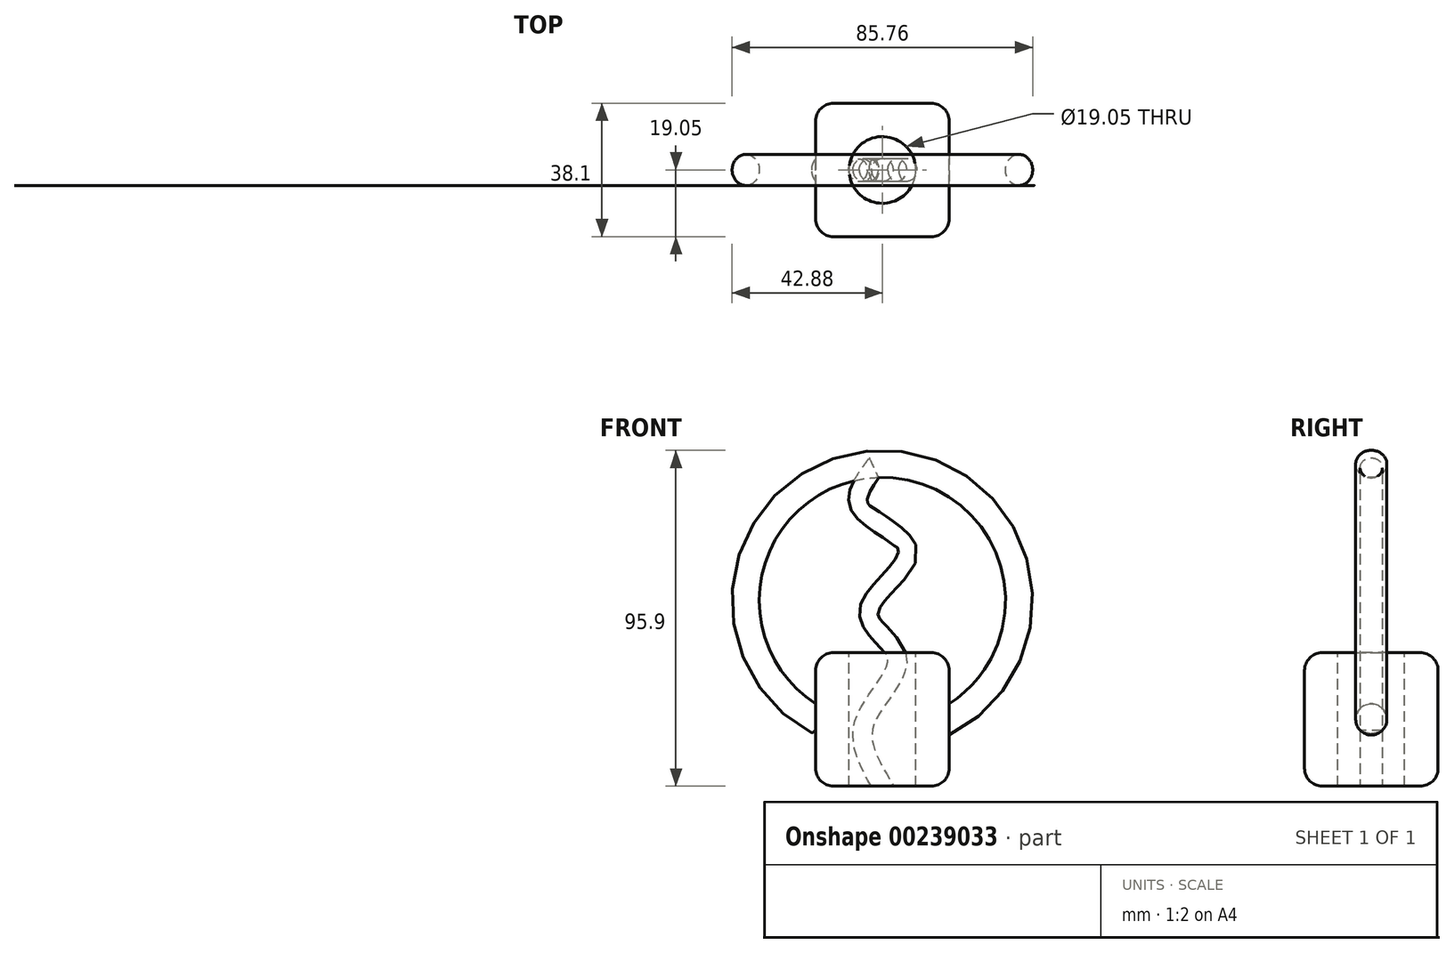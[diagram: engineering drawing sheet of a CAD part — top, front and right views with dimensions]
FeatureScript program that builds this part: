
annotation { "Feature Type Name" : "Feature", "Feature Type Description" : "" }
export const myFeature = defineFeature(function(context is Context, id is Id, definition is map)
    precondition{}
    {
        {
            var Q0;
            Q0=qCreatedBy(makeId("Front.planeOp"),FACE);
            var sketch = newSketch(context, id + "F0", { "sketchPlane" : qUnion([Q0])});
            skLineSegment(sketch, "E0", {"start": v(-38.1, 0) * mm, "end": v(-38.1, 38.1) * mm});
            skLineSegment(sketch, "E1", {"start": v(-38.1, 38.1) * mm, "end": v(0, 38.1) * mm});
            skLineSegment(sketch, "E2", {"start": v(0, 38.1) * mm, "end": v(0, 0) * mm});
            skLineSegment(sketch, "E3", {"start": v(0, 0) * mm, "end": v(-38.1, 0) * mm});
            skSolve(sketch);
        }
        {
            var Q0;
            Q0 = qSketchRegion(id + "F0", true);
            extrude(context, id + "F1", {"entities" : qUnion([Q0]), "depth" : 19.05 * mm});
        }
        {
            var Q0;
            Q0=makeQuery(id+"F1.opExtrude","CAP_FACE",FACE,{"disambiguationData":[OSD([sQuery(id+"F0.wireOp",EDGE,"E0"),sQuery(id+"F0.wireOp",EDGE,"E1"),sQuery(id+"F0.wireOp",EDGE,"E2"),sQuery(id+"F0.wireOp",EDGE,"E3")])],"isStart":true});
            extrude(context, id + "F2", {"entities" : qUnion([Q0]), "operationType" : NewBodyOperationType.ADD, "depth" : 19.05 * mm});
        }
        {
            var Q0;
            {var subQ0=sQuery(id+"F0.wireOp",EDGE,"E2");Q0=makeQuery(id+"F2.boolean.opBoolean","MERGE",FACE,{"derivedFrom":[makeQuery(id+"F1.opExtrude","SWEPT_FACE",FACE,{"disambiguationData":[OSD([subQ0])]}),makeQuery(id+"F2.opExtrude","SWEPT_FACE",FACE,{"disambiguationData":[OSD([subQ0])]})]});}
            var sketch = newSketch(context, id + "F3", { "sketchPlane" : qUnion([Q0])});
            skCircle(sketch, "E4", {"center": v(0, 19.05) * mm, "radius": 4.45 * mm});
            skPoint(sketch, "E4.centerSnap0", {"position": v(19.05, 19.05) * mm});
            skSolve(sketch);
        }
        {
            var Q0;
            Q0=qCreatedBy(makeId("Front.planeOp"),FACE);
            var sketch = newSketch(context, id + "F4", { "sketchPlane" : qUnion([Q0])});
            skPoint(sketch, "E5.third.point", {"position": v(-24.14, 91.63) * mm});
            skArc(sketch, "E6", {"start": v(0, 19.05) * mm, "mid": v(-20.48, 91.94) * mm, "end": v(-35.56, 17.75) * mm});
            skPoint(sketch, "E6.second.point", {"position": v(-40.73, 20.67) * mm});
            skPoint(sketch, "E6.third.point", {"position": v(-19.05, 91.97) * mm});
            skSolve(sketch);
        }
        {
            var Q0;
            Q0=makeQuery(id+"F3.imprint","IMPRINT",FACE,{"disambiguationData":[TD([[makeQuery(id+"F3.imprint","IMPRINT",EDGE,{"derivedFrom":sQuery(id+"F3.wireOp",EDGE,"E4")}),1.0]])]});
            var Q1;
            Q1=sQuery(id+"F4.wireOp",EDGE,"E6");
            sweep(context, id + "F5", {"operationType" : NewBodyOperationType.ADD, "profiles" : qUnion([Q0]), "path" : qUnion([Q1])});
        }
        {
            var Q0;
            Q0=makeQuery(id+"F1.opExtrude","CAP_EDGE",EDGE,{"disambiguationData":[OSD([sQuery(id+"F0.wireOp",EDGE,"E1")])],"isStart":false});
            var Q1;
            Q1=makeQuery(id+"F1.opExtrude","CAP_EDGE",EDGE,{"disambiguationData":[OSD([sQuery(id+"F0.wireOp",EDGE,"E2")])],"isStart":false});
            var Q2;
            {var subQ0=sQuery(id+"F0.wireOp",EDGE,"E2");var subQ1=sQuery(id+"F0.wireOp",EDGE,"E1");Q2=makeQuery(id+"F2.boolean.opBoolean","MERGE",EDGE,{"derivedFrom":[makeQuery(id+"F1.opExtrude","SWEPT_EDGE",EDGE,{"disambiguationData":[OSD([subQ1,subQ0])]}),makeQuery(id+"F2.opExtrude","SWEPT_EDGE",EDGE,{"disambiguationData":[OSD([subQ1,subQ0])]})]});}
            var Q3;
            Q3=makeQuery(id+"F2.opExtrude","CAP_EDGE",EDGE,{"disambiguationData":[OSD([sQuery(id+"F0.wireOp",EDGE,"E2")])],"isStart":false});
            var Q4;
            {var subQ0=sQuery(id+"F0.wireOp",EDGE,"E3");var subQ1=sQuery(id+"F0.wireOp",EDGE,"E2");Q4=makeQuery(id+"F2.boolean.opBoolean","MERGE",EDGE,{"derivedFrom":[makeQuery(id+"F1.opExtrude","SWEPT_EDGE",EDGE,{"disambiguationData":[OSD([subQ1,subQ0])]}),makeQuery(id+"F2.opExtrude","SWEPT_EDGE",EDGE,{"disambiguationData":[OSD([subQ1,subQ0])]})]});}
            var Q5;
            Q5=makeQuery(id+"F1.opExtrude","CAP_EDGE",EDGE,{"disambiguationData":[OSD([sQuery(id+"F0.wireOp",EDGE,"E3")])],"isStart":false});
            var Q6;
            Q6=makeQuery(id+"F1.opExtrude","CAP_EDGE",EDGE,{"disambiguationData":[OSD([sQuery(id+"F0.wireOp",EDGE,"E0")])],"isStart":false});
            var Q7;
            Q7=makeQuery(id+"F2.opExtrude","CAP_EDGE",EDGE,{"disambiguationData":[OSD([sQuery(id+"F0.wireOp",EDGE,"E0")])],"isStart":false});
            var Q8;
            Q8=makeQuery(id+"F2.opExtrude","CAP_EDGE",EDGE,{"disambiguationData":[OSD([sQuery(id+"F0.wireOp",EDGE,"E1")])],"isStart":false});
            var Q9;
            {var subQ0=sQuery(id+"F0.wireOp",EDGE,"E1");var subQ1=sQuery(id+"F0.wireOp",EDGE,"E0");Q9=makeQuery(id+"F2.boolean.opBoolean","MERGE",EDGE,{"derivedFrom":[makeQuery(id+"F1.opExtrude","SWEPT_EDGE",EDGE,{"disambiguationData":[OSD([subQ1,subQ0])]}),makeQuery(id+"F2.opExtrude","SWEPT_EDGE",EDGE,{"disambiguationData":[OSD([subQ1,subQ0])]})]});}
            var Q10;
            Q10=makeQuery(id+"F2.opExtrude","CAP_EDGE",EDGE,{"disambiguationData":[OSD([sQuery(id+"F0.wireOp",EDGE,"E3")])],"isStart":false});
            var Q11;
            {var subQ0=sQuery(id+"F0.wireOp",EDGE,"E3");var subQ1=sQuery(id+"F0.wireOp",EDGE,"E0");Q11=makeQuery(id+"F2.boolean.opBoolean","MERGE",EDGE,{"derivedFrom":[makeQuery(id+"F1.opExtrude","SWEPT_EDGE",EDGE,{"disambiguationData":[OSD([subQ1,subQ0])]}),makeQuery(id+"F2.opExtrude","SWEPT_EDGE",EDGE,{"disambiguationData":[OSD([subQ1,subQ0])]})]});}
            fillet(context, id + "F6", {"entities" : qUnion([Q0, Q1, Q2, Q3, Q4, Q5, Q6, Q7, Q8, Q9, Q10, Q11]), "radius" : 5.08 * mm, "tangentPropagation" : true, "allowEdgeOverflow" : false});
        }
        {
            var Q0;
            {var subQ0=sQuery(id+"F0.wireOp",EDGE,"E1");Q0=makeQuery(id+"F2.boolean.opBoolean","MERGE",FACE,{"derivedFrom":[makeQuery(id+"F1.opExtrude","SWEPT_FACE",FACE,{"disambiguationData":[OSD([subQ0])]}),makeQuery(id+"F2.opExtrude","SWEPT_FACE",FACE,{"disambiguationData":[OSD([subQ0])]})]});}
            var sketch = newSketch(context, id + "F7", { "sketchPlane" : qUnion([Q0])});
            skCircle(sketch, "E7", {"center": v(-19.05, 0) * mm, "radius": 9.53 * mm});
            skSolve(sketch);
        }
        {
            var Q0;
            Q0=makeQuery(id+"F7.imprint","IMPRINT",FACE,{"disambiguationData":[TD([[makeQuery(id+"F7.imprint","IMPRINT",EDGE,{"derivedFrom":sQuery(id+"F7.wireOp",EDGE,"E7")}),1.0]])]});
            extrude(context, id + "F8", {"entities" : qUnion([Q0]), "operationType" : NewBodyOperationType.REMOVE, "oppositeDirection" : true, "depth" : 62.48 * mm});
        }
        {
            var Q0;
            Q0=qCreatedBy(makeId("Front.planeOp"),FACE);
            var sketch = newSketch(context, id + "F9", { "sketchPlane" : qUnion([Q0])});
            skFitSpline(sketch, "E8", {"points": [v(-21.5, 90.85) * mm, v(-24.75, 79.04) * mm, v(-12.04, 66.66) * mm, v(-22.74, 49.94) * mm, v(-15.05, 36.57) * mm, v(-24.08, 18.17) * mm, v(-19.05, 0) * mm], "startDerivative": vector(-77.5, -108.48) * mm, "endDerivative": vector(61.54, -106.43) * mm});
            skSolve(sketch);
        }
        {
            var Q0;
            {var subQ0=sQuery(id+"F0.wireOp",EDGE,"E3");Q0=makeQuery(id+"F2.boolean.opBoolean","MERGE",FACE,{"derivedFrom":[makeQuery(id+"F1.opExtrude","SWEPT_FACE",FACE,{"disambiguationData":[OSD([subQ0])]}),makeQuery(id+"F2.opExtrude","SWEPT_FACE",FACE,{"disambiguationData":[OSD([subQ0])]})]});}
            var sketch = newSketch(context, id + "F10", { "sketchPlane" : qUnion([Q0])});
            skCircle(sketch, "E9", {"center": v(-19.05, 0) * mm, "radius": 3.18 * mm});
            skSolve(sketch);
        }
        {
            var Q0;
            Q0=makeQuery(id+"F10.imprint","IMPRINT",FACE,{"disambiguationData":[TD([[makeQuery(id+"F10.imprint","IMPRINT",EDGE,{"derivedFrom":sQuery(id+"F10.wireOp",EDGE,"E9")}),1.0]])]});
            var Q1;
            Q1=sQuery(id+"F9.wireOp",EDGE,"E8");
            sweep(context, id + "F11", {"profiles" : qUnion([Q0]), "path" : qUnion([Q1])});
        }
    });
